# Revit family: Shower-Rainhead-KOHLER-K-97167IN
name_source: partatom
category: Plumbing Fixtures
revit_build: Autodesk Revit 2017 (Build: 20160225_1515(x64)
units: mm (PartAtom-declared; Revit-internal decimal feet)

## family parameters
Cut with Voids When Loaded = No
Host = Face
OmniClass Number = 23.31.17.00
OmniClass Title = Showers
Part Type = Normal
Room Calculation Point = No
Round Connector Dimension = Use Diameter
Shared = No

## types (1)
- CP-Polished Chrome
    ADA Compliant = No
    Apparent Load = 0 VA
    Assembly Code = D2010700
    CW Connection = No
    Cold Water Inlet = Cold Water Inlet
    Date Modified = 05/24/2021
    Default Elevation = 42"
    Description = Square multi function rainpanel
    Drain Included = No
    Electrical Connector = Yes
    Electrical Note = One Dedicated Circuler Required
    Finish = Kohler-Metal-CP-Polished_Chrome
    Flow Rate = 0 GPM
    HW Connection = Yes
    Height = 1 9/16"
    Hot Water Inlet 1 = Tempered Water Inlet 1
    Hot Water Inlet 2 = Tempered Water Inlet 2
    Hot Water Inlet 3 = Tempered Water Inlet 3
    Hot Water Inlet 4 = Tempered Water Inlet 4
    Length = 19 11/16"
    Manufacturer = KOHLER Co.
    Master Format 2014 = 22 42 23
    Master Format 2014 Name = Residential Showers
    Material = Beass Construction
    Model = K-97167IN-CP
    Pressure = 0.00 psi
    Product Page URL = https://www.kohler.co.in
    Type = 1
    URL = https://www.kohler.co.in
    Vent Connection = No
    Voltage = 12 V
    Waste Connection = No
    Waste Water Outlet = Waste Water Outlet
    WaterSense Certified = No
    Width = 19 11/16"

## geometry (parser evidence)
native form markers: Sweep x4
no freeform markers — native parametric forms only
